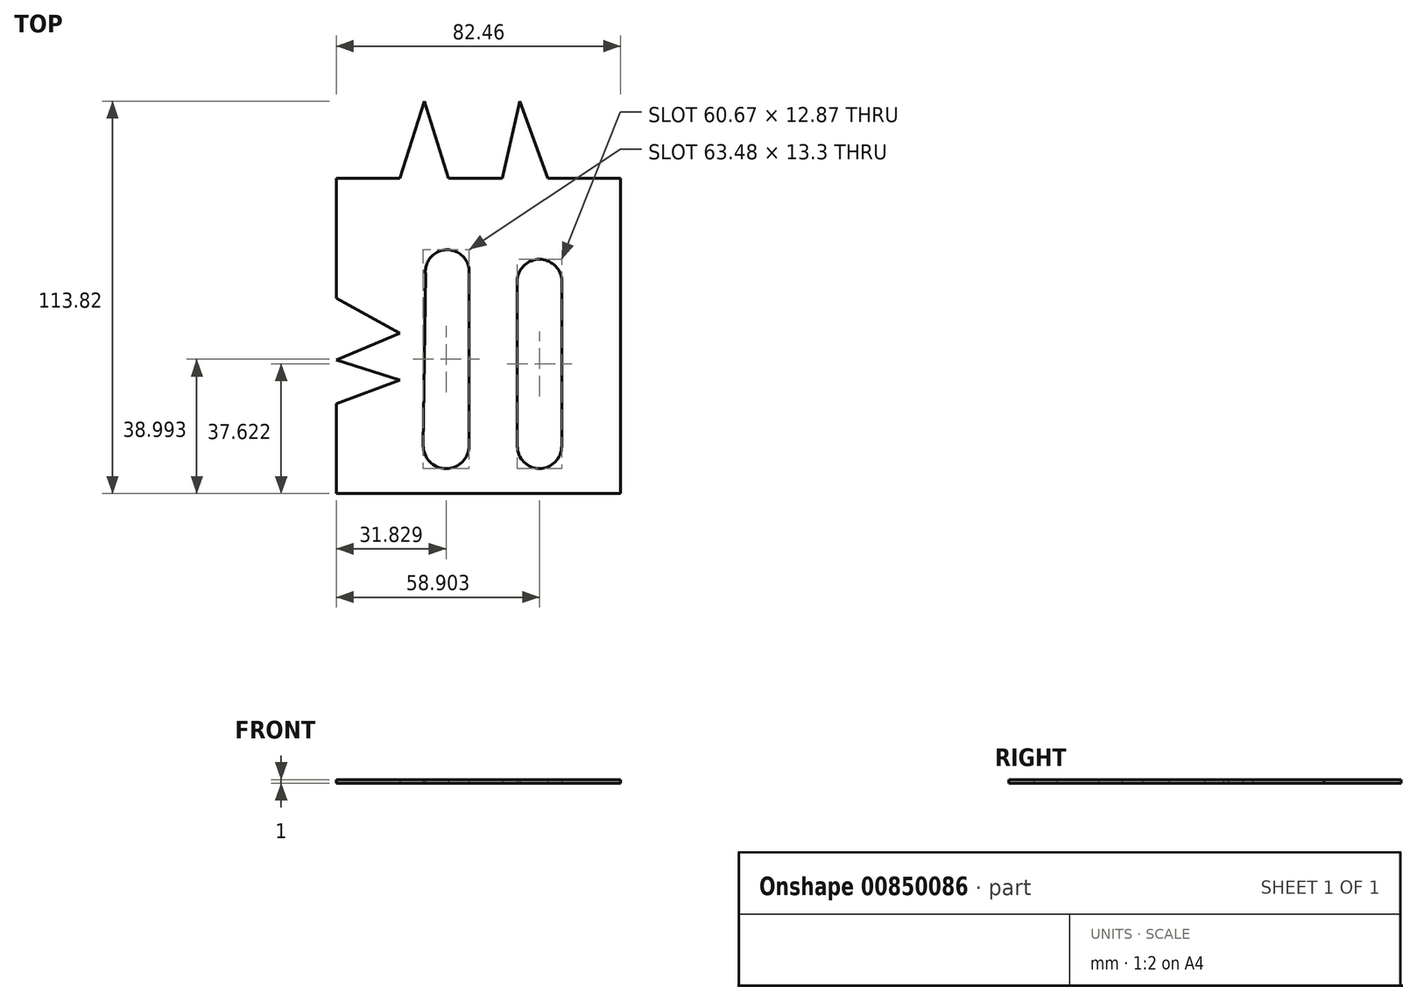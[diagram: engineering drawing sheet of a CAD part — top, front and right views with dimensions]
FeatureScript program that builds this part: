
annotation { "Feature Type Name" : "Feature", "Feature Type Description" : "" }
export const myFeature = defineFeature(function(context is Context, id is Id, definition is map)
    precondition{}
    {
        {
            var Q0;
            Q0=qCreatedBy(makeId("Top.planeOp"),FACE);
            var sketch = newSketch(context, id + "F0", { "sketchPlane" : qUnion([Q0])});
            skPoint(sketch, "E0.middle", {"position": v(0, 0) * mm});
            skLineSegment(sketch, "E1", {"start": v(20.7, 75) * mm, "end": v(28.88, 52.64) * mm});
            skLineSegment(sketch, "E2", {"start": v(28.88, 52.64) * mm, "end": v(50, 52.64) * mm});
            skLineSegment(sketch, "E3", {"start": v(20.7, 75) * mm, "end": v(15.59, 52.64) * mm});
            skLineSegment(sketch, "E4", {"start": v(15.59, 52.64) * mm, "end": v(0, 52.64) * mm});
            skLineSegment(sketch, "E5", {"start": v(0, 52.64) * mm, "end": v(-6.9, 75) * mm});
            skLineSegment(sketch, "E6", {"start": v(-6.9, 75) * mm, "end": v(-14.05, 52.64) * mm});
            skLineSegment(sketch, "E7", {"start": v(-14.05, 52.64) * mm, "end": v(-32.46, 52.64) * mm});
            skLineSegment(sketch, "E8", {"start": v(-32.46, 52.64) * mm, "end": v(-32.46, 17.89) * mm});
            skLineSegment(sketch, "E9", {"start": v(-32.46, 17.89) * mm, "end": v(-14.05, 7.67) * mm});
            skLineSegment(sketch, "E10", {"start": v(-14.05, 7.67) * mm, "end": v(-32.46, 0) * mm});
            skLineSegment(sketch, "E11", {"start": v(-32.46, 0) * mm, "end": v(-14.05, -5.89) * mm});
            skLineSegment(sketch, "E12", {"start": v(-14.05, -5.89) * mm, "end": v(-32.46, -12.78) * mm});
            skArc(sketch, "E13", {"start": v(32.88, 23.45) * mm, "mid": v(26.44, 29.14) * mm, "end": v(20, 23.45) * mm});
            skLineSegment(sketch, "E14", {"start": v(20, 23.45) * mm, "end": v(20, -25.1) * mm});
            skArc(sketch, "E15", {"start": v(20, -25.1) * mm, "mid": v(26.44, -31.53) * mm, "end": v(32.88, -25.1) * mm});
            skLineSegment(sketch, "E16", {"start": v(32.88, 23.45) * mm, "end": v(32.88, -25.1) * mm});
            skArc(sketch, "E17", {"start": v(6.02, 24.8) * mm, "mid": v(-0.24, 31.91) * mm, "end": v(-6.63, 24.93) * mm});
            skLineSegment(sketch, "E18", {"start": v(6.02, 24.8) * mm, "end": v(6.02, -24.92) * mm});
            skArc(sketch, "E19", {"start": v(-7.28, -24.92) * mm, "mid": v(-0.63, -31.57) * mm, "end": v(6.02, -24.92) * mm});
            skLineSegment(sketch, "E20", {"start": v(-6.63, 24.93) * mm, "end": v(-7.28, -24.92) * mm});
            skLineSegment(sketch, "E21", {"start": v(50, 52.64) * mm, "end": v(50, -39.47) * mm});
            skLineSegment(sketch, "E22", {"start": v(-32.46, -12.78) * mm, "end": v(-32.46, -38.82) * mm});
            skLineSegment(sketch, "E23", {"start": v(-32.46, -38.82) * mm, "end": v(50, -38.82) * mm});
            skSolve(sketch);
        }
        {
            var Q0;
            Q0 = qSketchRegion(id + "F0", true);
            extrude(context, id + "F1", {"entities" : qUnion([Q0]), "depth" : 1 * mm, "offsetDistance" : 25 * mm});
        }
    });
